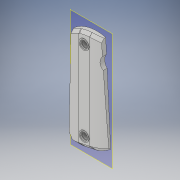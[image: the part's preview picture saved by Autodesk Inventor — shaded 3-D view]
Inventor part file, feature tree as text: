
AUTODESK INVENTOR PART (.ipt)
format: ipt  version: 2018.3 (Build 223284000, 284)  size: 293,376 bytes
history: native  units: in
note: dims shown in document units (in); Inventor stores cm internally (conversion verified against a paired STEP export)
features: extrude x7, sketch x3, chamfer x2, plane x2
ambient origin geometry x8: Origin, YZ Plane, XZ Plane, XY Plane, X Axis, Y Axis, Z Axis, Center Point
bodies: Solid1 (feature_tree)
feature tree (14):
  sketch  "Sketch1"  dims[d0=1.22in d1=0.72in]
  extrude  "Extrusion1"  Depth=0.72in
  extrude  "Extrusion2"  Depth=0.36in
  extrude  "Extrusion3"  Depth=0.1175in
  chamfer  "Chamfer1"  Distance=3.074in
  chamfer  "Chamfer2"  Distance=0.7009in
  extrude  "Extrusion4"  Depth=0.1175in
  plane  "Work Plane2"
  extrude  "Extrusion5"  Depth=0.1175in
  extrude  "Extrusion6"  Depth=0.1175in
  plane  "Work Plane3"
  extrude  "Extrusion7"  Depth=0.1175in
  sketch  "Sketch3"  dims[d2=0.91in d3=0.36in]
  sketch  "Sketch4"  dims[d4=1.542in d5=1.396in d6=3.074in d7=0.7009in d8=0.68in d9=0.63in d10=0.74in d11=1.182in d12=0.5in d13=0.25in d14=2.72in d15=0.24in d16=0.0in d17=0.38in d18=0.38in d19=0.26in d20=0.0in d25=0.06in d26=2.06in d27=0.0183in d28=2.06in d29=0.0183in d30=10.0725in d31=0.0in d32=0.225in d33=0.125in d34=45.0deg d42=0.1in d43=0.125in d44=45.0deg d45=0.238in d46=0.295in d47=0.238in d48=0.295in d49=0.885in d50=0.0in d51=0.0in d52=0.055in d53=0.0in d54=0.055in d55=0.0in d56=0.0in d57=0.1in d58=0.1175in d59=-0.1031in]
